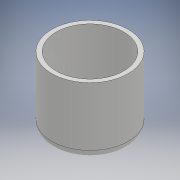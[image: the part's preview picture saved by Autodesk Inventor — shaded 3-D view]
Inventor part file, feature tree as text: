
AUTODESK INVENTOR PART (.ipt)
format: ipt  version: 2017 (Build 210142000, 142)  size: 124,928 bytes
history: native  units: mm
features: extrude x3, sketch x3, fillet x1
ambient origin geometry x8: Origin, YZ Plane, XZ Plane, XY Plane, X Axis, Y Axis, Z Axis, Center Point
bodies: Solid1 (feature_tree)
feature tree (7):
  extrude  "Extrusion1"  Depth=76.0mm
  extrude  "Extrusion2"  Depth=9.0mm
  fillet  "Fillet1"  Radius=8.0mm
  extrude  "Extrusion3"  [1 undecoded]
  sketch  "Sketch1"  dims[d2=75.0mm d3=0.0mm d4=76.0mm]
  sketch  "Sketch2"  dims[d5=71.0mm d6=0.0mm d7=9.0mm d8=8.0mm]
  sketch  "Sketch4"  dims[d9=10.0mm d10=0.0mm]
note: 1 required parameter value undecoded (feature->parameter linkage not recoverable at this tier; creation-order binding heuristic only, values carry confidence <= 0.55)
